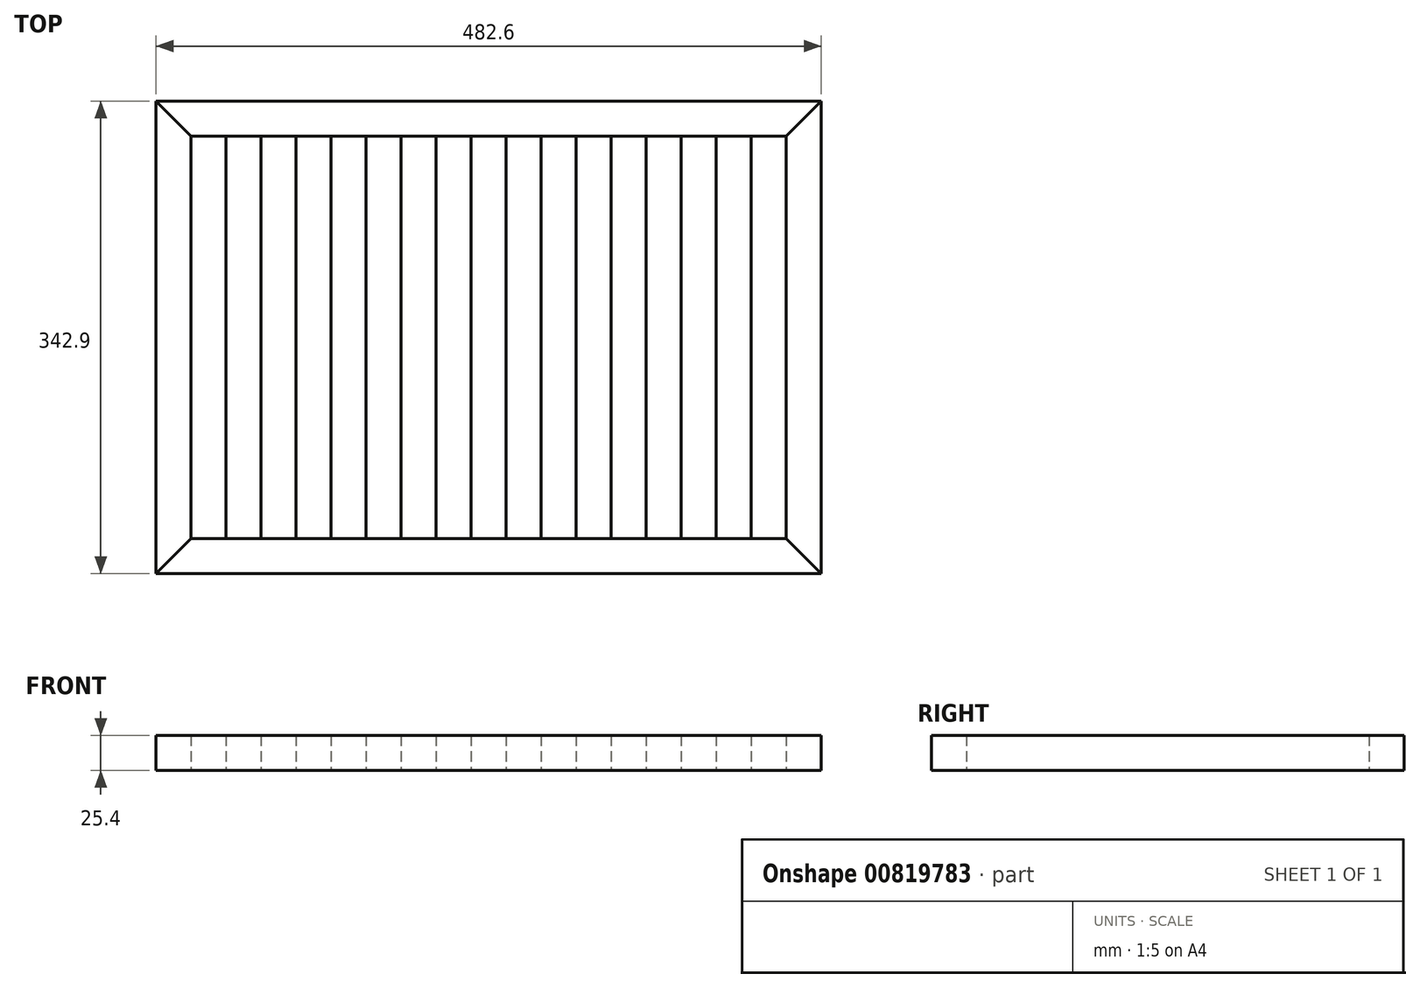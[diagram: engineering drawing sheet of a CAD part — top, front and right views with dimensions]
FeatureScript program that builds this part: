
annotation { "Feature Type Name" : "Feature", "Feature Type Description" : "" }
export const myFeature = defineFeature(function(context is Context, id is Id, definition is map)
    precondition{}
    {
        {
            var Q0;
            Q0=qCreatedBy(makeId("Top.planeOp"),FACE);
            var sketch = newSketch(context, id + "F0", { "sketchPlane" : qUnion([Q0])});
            skLineSegment(sketch, "E0.bottom", {"start": v(-241.3, -171.45) * mm, "end": v(241.3, -171.45) * mm});
            skLineSegment(sketch, "E0.top", {"start": v(-241.3, 171.45) * mm, "end": v(241.3, 171.45) * mm});
            skLineSegment(sketch, "E0.left", {"start": v(-241.3, -171.45) * mm, "end": v(-241.3, 171.45) * mm});
            skLineSegment(sketch, "E0.right", {"start": v(241.3, -171.45) * mm, "end": v(241.3, 171.45) * mm});
            skLineSegment(sketch, "E1.0", {"start": v(-215.9, -146.05) * mm, "end": v(-215.9, 146.05) * mm});
            skLineSegment(sketch, "E1.1", {"start": v(-215.9, -146.05) * mm, "end": v(215.9, -146.05) * mm});
            skLineSegment(sketch, "E1.2", {"start": v(215.9, -146.05) * mm, "end": v(215.9, 146.05) * mm});
            skLineSegment(sketch, "E1.3", {"start": v(-215.9, 146.05) * mm, "end": v(215.9, 146.05) * mm});
            skLineSegment(sketch, "E2", {"start": v(-215.9, 146.05) * mm, "end": v(-241.3, 171.45) * mm});
            skLineSegment(sketch, "E3", {"start": v(215.9, 146.05) * mm, "end": v(241.3, 171.45) * mm});
            skLineSegment(sketch, "E4", {"start": v(215.9, -146.05) * mm, "end": v(241.3, -171.45) * mm});
            skLineSegment(sketch, "E5", {"start": v(-241.3, -171.45) * mm, "end": v(-215.9, -146.05) * mm});
            skSolve(sketch);
        }
        {
            var Q0;
            Q0=makeQuery(id+"F0.imprint","IMPRINT",FACE,{"disambiguationData":[TD([[makeQuery(id+"F0.imprint","IMPRINT",EDGE,{"derivedFrom":sQuery(id+"F0.wireOp",EDGE,"E0.top")}),-1.0]])]});
            extrude(context, id + "F1", {"entities" : qUnion([Q0]), "depth" : 25.4 * mm, "offsetDistance" : 25.4 * mm});
        }
        {
            var Q0;
            Q0=makeQuery(id+"F0.imprint","IMPRINT",FACE,{"disambiguationData":[TD([[makeQuery(id+"F0.imprint","IMPRINT",EDGE,{"derivedFrom":sQuery(id+"F0.wireOp",EDGE,"E0.left")}),-1.0]])]});
            extrude(context, id + "F2", {"entities" : qUnion([Q0]), "depth" : 25.4 * mm, "offsetDistance" : 25.4 * mm});
        }
        {
            var Q0;
            Q0=makeQuery(id+"F0.imprint","IMPRINT",FACE,{"disambiguationData":[TD([[makeQuery(id+"F0.imprint","IMPRINT",EDGE,{"derivedFrom":sQuery(id+"F0.wireOp",EDGE,"E0.bottom")}),1.0]])]});
            extrude(context, id + "F3", {"entities" : qUnion([Q0]), "depth" : 25.4 * mm, "offsetDistance" : 25.4 * mm});
        }
        {
            var Q0;
            Q0=makeQuery(id+"F0.imprint","IMPRINT",FACE,{"disambiguationData":[TD([[makeQuery(id+"F0.imprint","IMPRINT",EDGE,{"derivedFrom":sQuery(id+"F0.wireOp",EDGE,"E0.right")}),1.0]])]});
            extrude(context, id + "F4", {"entities" : qUnion([Q0]), "depth" : 25.4 * mm, "offsetDistance" : 25.4 * mm});
        }
        {
            var Q0;
            Q0=qCreatedBy(makeId("Top.planeOp"),FACE);
            var sketch = newSketch(context, id + "F5", { "sketchPlane" : qUnion([Q0])});
            skLineSegment(sketch, "E6.bottom", {"start": v(-190.5, 146.05) * mm, "end": v(-165.1, 146.05) * mm});
            skLineSegment(sketch, "E6.top", {"start": v(-190.5, -146.05) * mm, "end": v(-165.1, -146.05) * mm});
            skLineSegment(sketch, "E6.left", {"start": v(-190.5, 146.05) * mm, "end": v(-190.5, -146.05) * mm});
            skLineSegment(sketch, "E6.right", {"start": v(-165.1, 146.05) * mm, "end": v(-165.1, -146.05) * mm});
            skLineSegment(sketch, "E7.1.0.0", {"start": v(-139.7, -146.05) * mm, "end": v(-114.3, -146.05) * mm});
            skLineSegment(sketch, "E7.1.0.1", {"start": v(-139.7, 146.05) * mm, "end": v(-139.7, -146.05) * mm});
            skLineSegment(sketch, "E7.1.0.2", {"start": v(-114.3, 146.05) * mm, "end": v(-114.3, -146.05) * mm});
            skLineSegment(sketch, "E7.1.0.3", {"start": v(-139.7, 146.05) * mm, "end": v(-114.3, 146.05) * mm});
            skLineSegment(sketch, "E7.2.0.0", {"start": v(-88.9, -146.05) * mm, "end": v(-63.5, -146.05) * mm});
            skLineSegment(sketch, "E7.2.0.1", {"start": v(-88.9, 146.05) * mm, "end": v(-88.9, -146.05) * mm});
            skLineSegment(sketch, "E7.2.0.2", {"start": v(-63.5, 146.05) * mm, "end": v(-63.5, -146.05) * mm});
            skLineSegment(sketch, "E7.2.0.3", {"start": v(-88.9, 146.05) * mm, "end": v(-63.5, 146.05) * mm});
            skLineSegment(sketch, "E7.3.0.0", {"start": v(-38.1, -146.05) * mm, "end": v(-12.7, -146.05) * mm});
            skLineSegment(sketch, "E7.3.0.1", {"start": v(-38.1, 146.05) * mm, "end": v(-38.1, -146.05) * mm});
            skLineSegment(sketch, "E7.3.0.2", {"start": v(-12.7, 146.05) * mm, "end": v(-12.7, -146.05) * mm});
            skLineSegment(sketch, "E7.3.0.3", {"start": v(-38.1, 146.05) * mm, "end": v(-12.7, 146.05) * mm});
            skLineSegment(sketch, "E7.4.0.0", {"start": v(12.7, -146.05) * mm, "end": v(38.1, -146.05) * mm});
            skLineSegment(sketch, "E7.4.0.1", {"start": v(12.7, 146.05) * mm, "end": v(12.7, -146.05) * mm});
            skLineSegment(sketch, "E7.4.0.2", {"start": v(38.1, 146.05) * mm, "end": v(38.1, -146.05) * mm});
            skLineSegment(sketch, "E7.4.0.3", {"start": v(12.7, 146.05) * mm, "end": v(38.1, 146.05) * mm});
            skLineSegment(sketch, "E7.5.0.0", {"start": v(63.5, -146.05) * mm, "end": v(88.9, -146.05) * mm});
            skLineSegment(sketch, "E7.5.0.1", {"start": v(63.5, 146.05) * mm, "end": v(63.5, -146.05) * mm});
            skLineSegment(sketch, "E7.5.0.2", {"start": v(88.9, 146.05) * mm, "end": v(88.9, -146.05) * mm});
            skLineSegment(sketch, "E7.5.0.3", {"start": v(63.5, 146.05) * mm, "end": v(88.9, 146.05) * mm});
            skLineSegment(sketch, "E7.6.0.0", {"start": v(114.3, -146.05) * mm, "end": v(139.7, -146.05) * mm});
            skLineSegment(sketch, "E7.6.0.1", {"start": v(114.3, 146.05) * mm, "end": v(114.3, -146.05) * mm});
            skLineSegment(sketch, "E7.6.0.2", {"start": v(139.7, 146.05) * mm, "end": v(139.7, -146.05) * mm});
            skLineSegment(sketch, "E7.6.0.3", {"start": v(114.3, 146.05) * mm, "end": v(139.7, 146.05) * mm});
            skLineSegment(sketch, "E7.7.0.0", {"start": v(165.1, -146.05) * mm, "end": v(190.5, -146.05) * mm});
            skLineSegment(sketch, "E7.7.0.1", {"start": v(165.1, 146.05) * mm, "end": v(165.1, -146.05) * mm});
            skLineSegment(sketch, "E7.7.0.2", {"start": v(190.5, 146.05) * mm, "end": v(190.5, -146.05) * mm});
            skLineSegment(sketch, "E7.7.0.3", {"start": v(165.1, 146.05) * mm, "end": v(190.5, 146.05) * mm});
            skLineSegment(sketch, "E7.direction1", {"start": v(-190.5, -146.05) * mm, "end": v(-139.7, -146.05) * mm, "construction": true});
            skSolve(sketch);
        }
        {
            var Q0;
            Q0=makeQuery(id+"F5.imprint","IMPRINT",FACE,{"disambiguationData":[TD([[makeQuery(id+"F5.imprint","IMPRINT",EDGE,{"derivedFrom":sQuery(id+"F5.wireOp",EDGE,"E6.bottom")}),-1.0]])]});
            extrude(context, id + "F6", {"entities" : qUnion([Q0]), "depth" : 25.4 * mm, "offsetDistance" : 25.4 * mm});
        }
        {
            var Q0;
            Q0=makeQuery(id+"F5.imprint","IMPRINT",FACE,{"disambiguationData":[TD([[makeQuery(id+"F5.imprint","IMPRINT",EDGE,{"derivedFrom":sQuery(id+"F5.wireOp",EDGE,"E7.1.0.0")}),1.0]])]});
            extrude(context, id + "F7", {"entities" : qUnion([Q0]), "depth" : 25.4 * mm, "offsetDistance" : 25.4 * mm});
        }
        {
            var Q0;
            Q0=makeQuery(id+"F5.imprint","IMPRINT",FACE,{"disambiguationData":[TD([[makeQuery(id+"F5.imprint","IMPRINT",EDGE,{"derivedFrom":sQuery(id+"F5.wireOp",EDGE,"E7.2.0.0")}),1.0]])]});
            extrude(context, id + "F8", {"entities" : qUnion([Q0]), "depth" : 25.4 * mm, "offsetDistance" : 25.4 * mm});
        }
        {
            var Q0;
            Q0=makeQuery(id+"F5.imprint","IMPRINT",FACE,{"disambiguationData":[TD([[makeQuery(id+"F5.imprint","IMPRINT",EDGE,{"derivedFrom":sQuery(id+"F5.wireOp",EDGE,"E7.3.0.0")}),1.0]])]});
            extrude(context, id + "F9", {"entities" : qUnion([Q0]), "depth" : 25.4 * mm, "offsetDistance" : 25.4 * mm});
        }
        {
            var Q0;
            Q0=makeQuery(id+"F5.imprint","IMPRINT",FACE,{"disambiguationData":[TD([[makeQuery(id+"F5.imprint","IMPRINT",EDGE,{"derivedFrom":sQuery(id+"F5.wireOp",EDGE,"E7.4.0.0")}),1.0]])]});
            extrude(context, id + "F10", {"entities" : qUnion([Q0]), "depth" : 25.4 * mm, "offsetDistance" : 25.4 * mm});
        }
        {
            var Q0;
            Q0=makeQuery(id+"F5.imprint","IMPRINT",FACE,{"disambiguationData":[TD([[makeQuery(id+"F5.imprint","IMPRINT",EDGE,{"derivedFrom":sQuery(id+"F5.wireOp",EDGE,"E7.5.0.0")}),1.0]])]});
            extrude(context, id + "F11", {"entities" : qUnion([Q0]), "depth" : 25.4 * mm, "offsetDistance" : 25.4 * mm});
        }
        {
            var Q0;
            Q0=makeQuery(id+"F5.imprint","IMPRINT",FACE,{"disambiguationData":[TD([[makeQuery(id+"F5.imprint","IMPRINT",EDGE,{"derivedFrom":sQuery(id+"F5.wireOp",EDGE,"E7.6.0.0")}),1.0]])]});
            extrude(context, id + "F12", {"entities" : qUnion([Q0]), "depth" : 25.4 * mm, "offsetDistance" : 25.4 * mm});
        }
        {
            var Q0;
            Q0=makeQuery(id+"F5.imprint","IMPRINT",FACE,{"disambiguationData":[TD([[makeQuery(id+"F5.imprint","IMPRINT",EDGE,{"derivedFrom":sQuery(id+"F5.wireOp",EDGE,"E7.7.0.0")}),1.0]])]});
            extrude(context, id + "F13", {"entities" : qUnion([Q0]), "depth" : 25.4 * mm, "offsetDistance" : 25.4 * mm});
        }
    });
